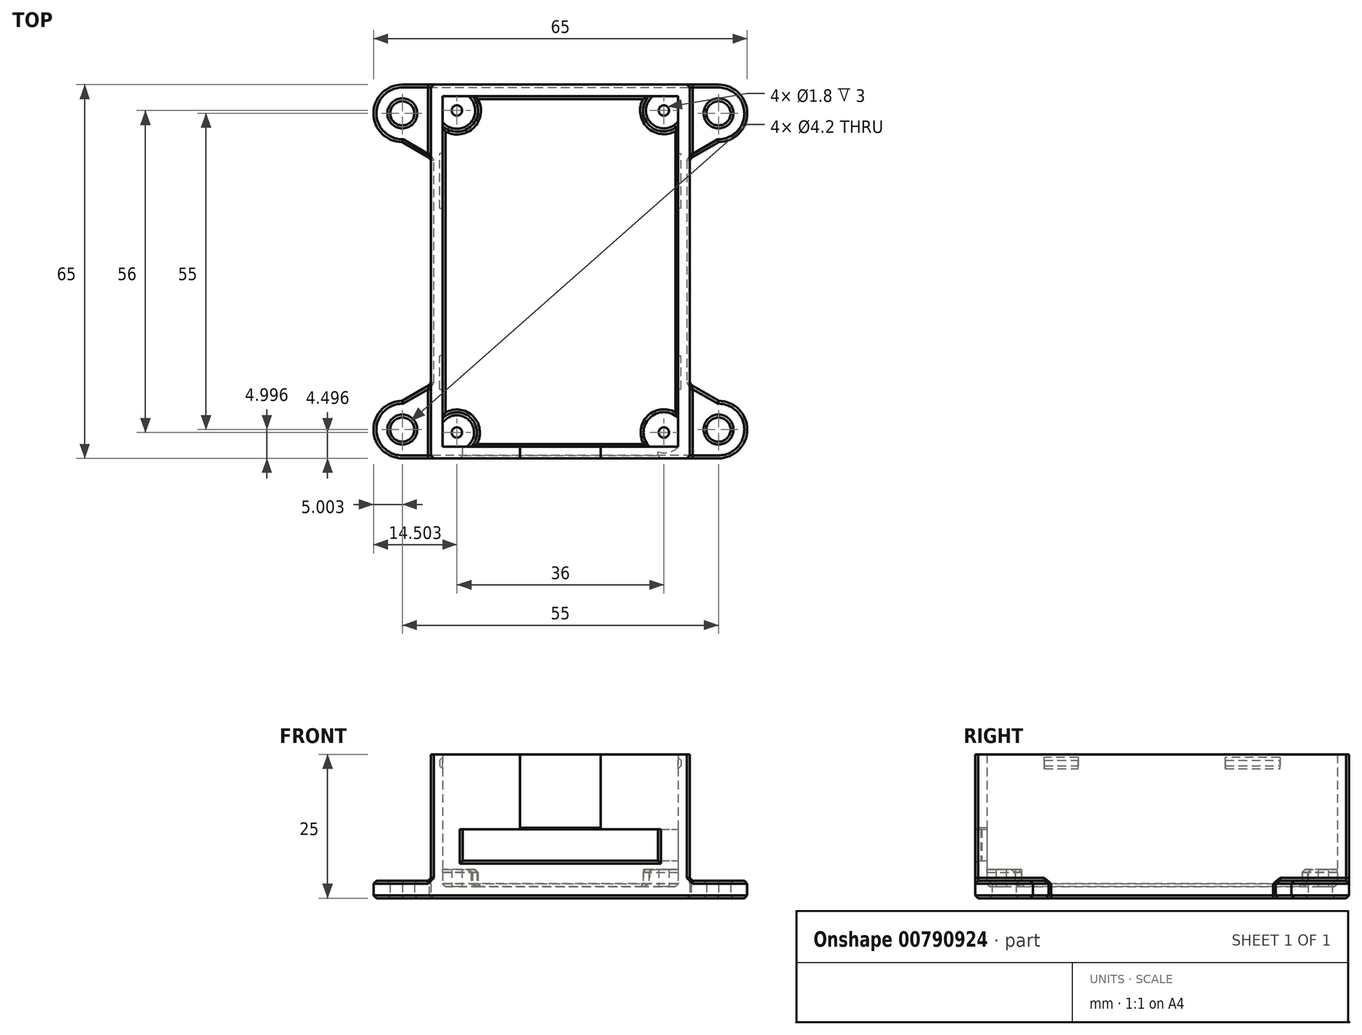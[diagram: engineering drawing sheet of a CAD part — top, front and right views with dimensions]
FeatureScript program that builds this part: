
annotation { "Feature Type Name" : "Feature", "Feature Type Description" : "" }
export const myFeature = defineFeature(function(context is Context, id is Id, definition is map)
    precondition{}
    {
        {
            var Q0;
            Q0=qCreatedBy(makeId("Top.planeOp"),FACE);
            var sketch = newSketch(context, id + "F0", { "sketchPlane" : qUnion([Q0])});
            skLineSegment(sketch, "E0.bottom", {"start": v(-31.58, 31.85) * mm, "end": v(9.42, 31.85) * mm});
            skLineSegment(sketch, "E0.top", {"start": v(-31.58, -29.15) * mm, "end": v(9.42, -29.15) * mm});
            skLineSegment(sketch, "E0.left", {"start": v(-31.58, 31.85) * mm, "end": v(-31.58, -29.15) * mm});
            skLineSegment(sketch, "E0.right", {"start": v(9.42, 31.85) * mm, "end": v(9.42, -29.15) * mm});
            skCircle(sketch, "E1", {"center": v(-29.08, 29.35) * mm, "radius": 0.9 * mm});
            skCircle(sketch, "E2", {"center": v(6.92, 29.35) * mm, "radius": 0.9 * mm});
            skCircle(sketch, "E3", {"center": v(-29.08, 29.35) * mm, "radius": 3.69 * mm});
            skCircle(sketch, "E4", {"center": v(6.92, 29.35) * mm, "radius": 3.62 * mm});
            skCircle(sketch, "E5", {"center": v(-29.08, -26.65) * mm, "radius": 0.9 * mm});
            skCircle(sketch, "E6", {"center": v(6.92, -26.65) * mm, "radius": 0.9 * mm});
            skCircle(sketch, "E7", {"center": v(-29.08, -26.65) * mm, "radius": 3.5 * mm});
            skCircle(sketch, "E8", {"center": v(6.92, -26.65) * mm, "radius": 3.54 * mm});
            skLineSegment(sketch, "E9.bottom", {"start": v(-33.58, 33.85) * mm, "end": v(11.42, 33.85) * mm});
            skLineSegment(sketch, "E9.top", {"start": v(-33.58, -31.15) * mm, "end": v(11.42, -31.15) * mm});
            skLineSegment(sketch, "E9.left", {"start": v(-33.58, 33.85) * mm, "end": v(-33.58, -31.15) * mm});
            skLineSegment(sketch, "E9.right", {"start": v(11.42, 33.85) * mm, "end": v(11.42, -31.15) * mm});
            skLineSegment(sketch, "E10.bottom", {"start": v(-32.08, -19.15) * mm, "end": v(9.92, -19.15) * mm});
            skLineSegment(sketch, "E10.top", {"start": v(-32.08, -13.29) * mm, "end": v(9.92, -13.29) * mm});
            skLineSegment(sketch, "E10.left", {"start": v(-32.08, -19.15) * mm, "end": v(-32.08, -13.29) * mm});
            skLineSegment(sketch, "E10.right", {"start": v(9.92, -19.15) * mm, "end": v(9.92, -13.29) * mm});
            skLineSegment(sketch, "E11.bottom", {"start": v(-32.08, 12.33) * mm, "end": v(9.92, 12.33) * mm});
            skLineSegment(sketch, "E11.top", {"start": v(-32.08, 21.85) * mm, "end": v(9.92, 21.85) * mm});
            skLineSegment(sketch, "E11.left", {"start": v(-32.08, 12.33) * mm, "end": v(-32.08, 21.85) * mm});
            skLineSegment(sketch, "E11.right", {"start": v(9.92, 12.33) * mm, "end": v(9.92, 21.85) * mm});
            skLineSegment(sketch, "E12.bottom", {"start": v(-28.08, -33.78) * mm, "end": v(5.92, -33.78) * mm});
            skLineSegment(sketch, "E12.top", {"start": v(-28.08, -29.15) * mm, "end": v(5.92, -29.15) * mm});
            skLineSegment(sketch, "E12.left", {"start": v(-28.08, -33.78) * mm, "end": v(-28.08, -29.15) * mm});
            skLineSegment(sketch, "E12.right", {"start": v(5.92, -33.78) * mm, "end": v(5.92, -29.15) * mm});
            skLineSegment(sketch, "E13.bottom", {"start": v(-18.08, -27.24) * mm, "end": v(-4.08, -27.24) * mm});
            skLineSegment(sketch, "E13.top", {"start": v(-18.08, -36.6) * mm, "end": v(-4.08, -36.6) * mm});
            skLineSegment(sketch, "E13.left", {"start": v(-18.08, -27.24) * mm, "end": v(-18.08, -36.6) * mm});
            skLineSegment(sketch, "E13.right", {"start": v(-4.08, -27.24) * mm, "end": v(-4.08, -36.6) * mm});
            skLineSegment(sketch, "E14", {"start": v(11.42, 33.85) * mm, "end": v(16.42, 33.85) * mm});
            skArc(sketch, "E15", {"start": v(16.42, 33.85) * mm, "mid": v(21.42, 28.85) * mm, "end": v(16.42, 23.85) * mm});
            skLineSegment(sketch, "E16", {"start": v(16.42, 23.85) * mm, "end": v(11.42, 20.96) * mm});
            skCircle(sketch, "E17", {"center": v(16.42, 28.85) * mm, "radius": 2.1 * mm});
            skLineSegment(sketch, "E18", {"start": v(-33.58, 33.85) * mm, "end": v(-38.58, 33.85) * mm});
            skArc(sketch, "E19", {"start": v(-38.58, 33.85) * mm, "mid": v(-43.58, 28.85) * mm, "end": v(-38.58, 23.85) * mm});
            skLineSegment(sketch, "E20", {"start": v(-38.58, 23.85) * mm, "end": v(-33.58, 20.96) * mm});
            skLineSegment(sketch, "E21", {"start": v(11.42, -31.15) * mm, "end": v(16.42, -31.15) * mm});
            skArc(sketch, "E22", {"start": v(16.42, -31.15) * mm, "mid": v(21.42, -26.15) * mm, "end": v(16.42, -21.15) * mm});
            skLineSegment(sketch, "E23", {"start": v(16.42, -21.15) * mm, "end": v(11.42, -18.27) * mm});
            skLineSegment(sketch, "E24", {"start": v(-33.58, -31.15) * mm, "end": v(-38.58, -31.15) * mm});
            skArc(sketch, "E25", {"start": v(-38.58, -31.15) * mm, "mid": v(-43.58, -26.15) * mm, "end": v(-38.58, -21.15) * mm});
            skLineSegment(sketch, "E26", {"start": v(-38.58, -21.15) * mm, "end": v(-33.58, -18.27) * mm});
            skCircle(sketch, "E27", {"center": v(-38.58, 28.85) * mm, "radius": 2.1 * mm});
            skCircle(sketch, "E28", {"center": v(-38.58, -26.15) * mm, "radius": 2.1 * mm});
            skCircle(sketch, "E29", {"center": v(16.42, -26.15) * mm, "radius": 2.1 * mm});
            skSolve(sketch);
        }
        {
            var Q0;
            Q0=makeQuery(id+"F0.imprint","IMPRINT",FACE,{"disambiguationData":[TD([[makeQuery(id+"F0.imprint","IMPRINT",EDGE,{"derivedFrom":sQuery(id+"F0.wireOp",EDGE,"E9.bottom")}),-1.0]])]});
            var Q1;
            {var subQ0=sQuery(id+"F0.wireOp",EDGE,"E0.right");var subQ1=sQuery(id+"F0.wireOp",EDGE,"E0.bottom");var subQ2=makeQuery(id+"F0.imprint","INTERSECT",VERTEX,{"derivedFrom":[subQ1,subQ0]});Q1=makeQuery(id+"F0.imprint","IMPRINT",FACE,{"disambiguationData":[TD([[makeQuery(id+"F0.imprint","IMPRINT",EDGE,{"disambiguationData":[TD([[subQ2,1.0]])],"derivedFrom":subQ1}),1.0]])]});}
            var Q2;
            {var subQ0=sQuery(id+"F0.wireOp",EDGE,"E7");var subQ1=sQuery(id+"F0.wireOp",EDGE,"E0.top");var subQ2=makeQuery(id+"F0.imprint","INTERSECT",VERTEX,{"disambiguationData":[OD(1.0)],"derivedFrom":[subQ1,subQ0]});Q2=makeQuery(id+"F0.imprint","IMPRINT",FACE,{"disambiguationData":[TD([[makeQuery(id+"F0.imprint","IMPRINT",EDGE,{"disambiguationData":[TD([[subQ2,-1.0]])],"derivedFrom":subQ1}),1.0]])]});}
            var Q3;
            {var subQ0=sQuery(id+"F0.wireOp",EDGE,"E13.right");var subQ1=sQuery(id+"F0.wireOp",EDGE,"E0.top");var subQ2=makeQuery(id+"F0.imprint","INTERSECT",VERTEX,{"derivedFrom":[subQ1,subQ0]});Q3=makeQuery(id+"F0.imprint","IMPRINT",FACE,{"disambiguationData":[TD([[makeQuery(id+"F0.imprint","IMPRINT",EDGE,{"disambiguationData":[TD([[subQ2,-1.0]])],"derivedFrom":subQ1}),1.0]])]});}
            var Q4;
            Q4=makeQuery(id+"F0.imprint","IMPRINT",FACE,{"disambiguationData":[TD([[makeQuery(id+"F0.imprint","IMPRINT",EDGE,{"derivedFrom":sQuery(id+"F0.wireOp",EDGE,"E5")}),-1.0]])]});
            var Q5;
            Q5=makeQuery(id+"F0.imprint","IMPRINT",FACE,{"disambiguationData":[TD([[makeQuery(id+"F0.imprint","IMPRINT",EDGE,{"derivedFrom":sQuery(id+"F0.wireOp",EDGE,"E1")}),-1.0]])]});
            var Q6;
            {var subQ0=sQuery(id+"F0.wireOp",EDGE,"E0.left");var subQ1=sQuery(id+"F0.wireOp",EDGE,"E0.bottom");var subQ2=makeQuery(id+"F0.imprint","INTERSECT",VERTEX,{"derivedFrom":[subQ1,subQ0]});Q6=makeQuery(id+"F0.imprint","IMPRINT",FACE,{"disambiguationData":[TD([[makeQuery(id+"F0.imprint","IMPRINT",EDGE,{"disambiguationData":[TD([[subQ2,-1.0]])],"derivedFrom":subQ1}),1.0]])]});}
            var Q7;
            {var subQ0=sQuery(id+"F0.wireOp",EDGE,"E13.left");var subQ1=sQuery(id+"F0.wireOp",EDGE,"E0.top");var subQ2=makeQuery(id+"F0.imprint","INTERSECT",VERTEX,{"derivedFrom":[subQ1,subQ0]});Q7=makeQuery(id+"F0.imprint","IMPRINT",FACE,{"disambiguationData":[TD([[makeQuery(id+"F0.imprint","IMPRINT",EDGE,{"disambiguationData":[TD([[subQ2,-1.0]])],"derivedFrom":subQ1}),-1.0]])]});}
            var Q8;
            {var subQ0=sQuery(id+"F0.wireOp",EDGE,"E11.top");var subQ1=sQuery(id+"F0.wireOp",EDGE,"E0.left");var subQ2=makeQuery(id+"F0.imprint","INTERSECT",VERTEX,{"derivedFrom":[subQ1,subQ0]});Q8=makeQuery(id+"F0.imprint","IMPRINT",FACE,{"disambiguationData":[TD([[makeQuery(id+"F0.imprint","IMPRINT",EDGE,{"disambiguationData":[TD([[subQ2,-1.0]])],"derivedFrom":subQ1}),1.0]])]});}
            var Q9;
            {var subQ3=sQuery(id+"F0.wireOp",EDGE,"E7");var subQ6=sQuery(id+"F0.wireOp",EDGE,"E0.top");var subQ9=makeQuery(id+"F0.imprint","INTERSECT",VERTEX,{"disambiguationData":[OD(1.0)],"derivedFrom":[subQ6,subQ3]});Q9=makeQuery(id+"F0.imprint","IMPRINT",FACE,{"disambiguationData":[TD([[makeQuery(id+"F0.imprint","IMPRINT",EDGE,{"disambiguationData":[TD([[subQ9,-1.0]])],"derivedFrom":subQ6}),-1.0]])]});}
            var Q10;
            Q10=makeQuery(id+"F0.imprint","IMPRINT",FACE,{"disambiguationData":[TD([[makeQuery(id+"F0.imprint","IMPRINT",EDGE,{"derivedFrom":sQuery(id+"F0.wireOp",EDGE,"E2")}),-1.0]])]});
            var Q11;
            {var subQ0=sQuery(id+"F0.wireOp",EDGE,"E10.top");var subQ1=sQuery(id+"F0.wireOp",EDGE,"E0.left");var subQ2=makeQuery(id+"F0.imprint","INTERSECT",VERTEX,{"derivedFrom":[subQ1,subQ0]});Q11=makeQuery(id+"F0.imprint","IMPRINT",FACE,{"disambiguationData":[TD([[makeQuery(id+"F0.imprint","IMPRINT",EDGE,{"disambiguationData":[TD([[subQ2,-1.0]])],"derivedFrom":subQ1}),1.0]])]});}
            var Q12;
            {var subQ5=sQuery(id+"F0.wireOp",EDGE,"E13.bottom");Q12=makeQuery(id+"F0.imprint","IMPRINT",FACE,{"disambiguationData":[TD([[makeQuery(id+"F0.imprint","IMPRINT",EDGE,{"derivedFrom":subQ5}),-1.0]])]});}
            var Q13;
            {var subQ0=sQuery(id+"F0.wireOp",EDGE,"E11.bottom");var subQ1=sQuery(id+"F0.wireOp",EDGE,"E0.left");var subQ2=makeQuery(id+"F0.imprint","INTERSECT",VERTEX,{"derivedFrom":[subQ1,subQ0]});Q13=makeQuery(id+"F0.imprint","IMPRINT",FACE,{"disambiguationData":[TD([[makeQuery(id+"F0.imprint","IMPRINT",EDGE,{"disambiguationData":[TD([[subQ2,-1.0]])],"derivedFrom":subQ1}),1.0]])]});}
            var Q14;
            {var subQ0=sQuery(id+"F0.wireOp",EDGE,"E13.left");var subQ1=sQuery(id+"F0.wireOp",EDGE,"E0.top");var subQ2=makeQuery(id+"F0.imprint","INTERSECT",VERTEX,{"derivedFrom":[subQ1,subQ0]});Q14=makeQuery(id+"F0.imprint","IMPRINT",FACE,{"disambiguationData":[TD([[makeQuery(id+"F0.imprint","IMPRINT",EDGE,{"disambiguationData":[TD([[subQ2,-1.0]])],"derivedFrom":subQ1}),1.0]])]});}
            var Q15;
            Q15=makeQuery(id+"F0.imprint","IMPRINT",FACE,{"disambiguationData":[TD([[makeQuery(id+"F0.imprint","IMPRINT",EDGE,{"derivedFrom":sQuery(id+"F0.wireOp",EDGE,"E6")}),-1.0]])]});
            var Q16;
            {var subQ14=sQuery(id+"F0.wireOp",EDGE,"E13.bottom");Q16=makeQuery(id+"F0.imprint","IMPRINT",FACE,{"disambiguationData":[TD([[makeQuery(id+"F0.imprint","IMPRINT",EDGE,{"derivedFrom":subQ14}),1.0]])]});}
            var Q17;
            {var subQ0=sQuery(id+"F0.wireOp",EDGE,"E3");var subQ1=sQuery(id+"F0.wireOp",EDGE,"E0.bottom");var subQ2=makeQuery(id+"F0.imprint","INTERSECT",VERTEX,{"derivedFrom":[subQ1,subQ0]});Q17=makeQuery(id+"F0.imprint","IMPRINT",FACE,{"disambiguationData":[TD([[makeQuery(id+"F0.imprint","IMPRINT",EDGE,{"disambiguationData":[TD([[subQ2,-1.0]])],"derivedFrom":subQ1}),-1.0]])]});}
            var Q18;
            {var subQ3=sQuery(id+"F0.wireOp",EDGE,"E13.right");var subQ7=sQuery(id+"F0.wireOp",EDGE,"E0.top");var subQ9=makeQuery(id+"F0.imprint","INTERSECT",VERTEX,{"derivedFrom":[subQ7,subQ3]});Q18=makeQuery(id+"F0.imprint","IMPRINT",FACE,{"disambiguationData":[TD([[makeQuery(id+"F0.imprint","IMPRINT",EDGE,{"disambiguationData":[TD([[subQ9,-1.0]])],"derivedFrom":subQ7}),-1.0]])]});}
            var Q19;
            {var subQ0=sQuery(id+"F0.wireOp",EDGE,"E7");var subQ1=sQuery(id+"F0.wireOp",EDGE,"E0.left");var subQ2=makeQuery(id+"F0.imprint","INTERSECT",VERTEX,{"disambiguationData":[OD(0.0)],"derivedFrom":[subQ1,subQ0]});Q19=makeQuery(id+"F0.imprint","IMPRINT",FACE,{"disambiguationData":[TD([[makeQuery(id+"F0.imprint","IMPRINT",EDGE,{"disambiguationData":[TD([[subQ2,-1.0]])],"derivedFrom":subQ1}),-1.0]])]});}
            var Q20;
            {var subQ0=sQuery(id+"F0.wireOp",EDGE,"E12.left");var subQ1=sQuery(id+"F0.wireOp",EDGE,"E0.top");var subQ2=makeQuery(id+"F0.imprint","INTERSECT",VERTEX,{"derivedFrom":[subQ1,subQ0]});Q20=makeQuery(id+"F0.imprint","IMPRINT",FACE,{"disambiguationData":[TD([[makeQuery(id+"F0.imprint","IMPRINT",EDGE,{"disambiguationData":[TD([[subQ2,-1.0]])],"derivedFrom":subQ1}),1.0]])]});}
            var Q21;
            {var subQ0=sQuery(id+"F0.wireOp",EDGE,"E8");var subQ1=sQuery(id+"F0.wireOp",EDGE,"E0.top");var subQ2=makeQuery(id+"F0.imprint","INTERSECT",VERTEX,{"derivedFrom":[subQ1,subQ0]});Q21=makeQuery(id+"F0.imprint","IMPRINT",FACE,{"disambiguationData":[TD([[makeQuery(id+"F0.imprint","IMPRINT",EDGE,{"disambiguationData":[TD([[subQ2,-1.0]])],"derivedFrom":subQ1}),-1.0]])]});}
            var Q22;
            {var subQ5=sQuery(id+"F0.wireOp",EDGE,"E11.right");Q22=makeQuery(id+"F0.imprint","IMPRINT",FACE,{"disambiguationData":[TD([[makeQuery(id+"F0.imprint","IMPRINT",EDGE,{"derivedFrom":subQ5}),1.0]])]});}
            var Q23;
            {var subQ5=sQuery(id+"F0.wireOp",EDGE,"E10.right");Q23=makeQuery(id+"F0.imprint","IMPRINT",FACE,{"disambiguationData":[TD([[makeQuery(id+"F0.imprint","IMPRINT",EDGE,{"derivedFrom":subQ5}),1.0]])]});}
            var Q24;
            {var subQ5=sQuery(id+"F0.wireOp",EDGE,"E10.left");Q24=makeQuery(id+"F0.imprint","IMPRINT",FACE,{"disambiguationData":[TD([[makeQuery(id+"F0.imprint","IMPRINT",EDGE,{"derivedFrom":subQ5}),-1.0]])]});}
            var Q25;
            {var subQ5=sQuery(id+"F0.wireOp",EDGE,"E11.left");Q25=makeQuery(id+"F0.imprint","IMPRINT",FACE,{"disambiguationData":[TD([[makeQuery(id+"F0.imprint","IMPRINT",EDGE,{"derivedFrom":subQ5}),-1.0]])]});}
            var Q26;
            {var subQ1=sQuery(id+"F0.wireOp",EDGE,"E0.top");var subQ3=sQuery(id+"F0.wireOp",EDGE,"E12.right");var subQ4=makeQuery(id+"F0.imprint","INTERSECT",VERTEX,{"derivedFrom":[subQ1,subQ3]});Q26=makeQuery(id+"F0.imprint","IMPRINT",FACE,{"disambiguationData":[TD([[makeQuery(id+"F0.imprint","IMPRINT",EDGE,{"disambiguationData":[TD([[subQ4,1.0]])],"derivedFrom":subQ3}),-1.0]])]});}
            var Q27;
            {var subQ0=sQuery(id+"F0.wireOp",EDGE,"E8");var subQ1=sQuery(id+"F0.wireOp",EDGE,"E0.right");var subQ3=makeQuery(id+"F0.imprint","INTERSECT",VERTEX,{"derivedFrom":[subQ1,subQ0]});Q27=makeQuery(id+"F0.imprint","IMPRINT",FACE,{"disambiguationData":[TD([[makeQuery(id+"F0.imprint","IMPRINT",EDGE,{"disambiguationData":[TD([[subQ3,-1.0]])],"derivedFrom":subQ1}),1.0]])]});}
            var Q28;
            {var subQ0=sQuery(id+"F0.wireOp",EDGE,"E12.left");var subQ1=sQuery(id+"F0.wireOp",EDGE,"E0.top");var subQ2=makeQuery(id+"F0.imprint","INTERSECT",VERTEX,{"derivedFrom":[subQ1,subQ0]});Q28=makeQuery(id+"F0.imprint","IMPRINT",FACE,{"disambiguationData":[TD([[makeQuery(id+"F0.imprint","IMPRINT",EDGE,{"disambiguationData":[TD([[subQ2,-1.0]])],"derivedFrom":subQ1}),-1.0]])]});}
            var Q29;
            {var subQ0=sQuery(id+"F0.wireOp",EDGE,"E8");var subQ1=sQuery(id+"F0.wireOp",EDGE,"E0.top");var subQ2=makeQuery(id+"F0.imprint","INTERSECT",VERTEX,{"derivedFrom":[subQ1,subQ0]});Q29=makeQuery(id+"F0.imprint","IMPRINT",FACE,{"disambiguationData":[TD([[makeQuery(id+"F0.imprint","IMPRINT",EDGE,{"disambiguationData":[TD([[subQ2,-1.0]])],"derivedFrom":subQ1}),1.0]])]});}
            var Q30;
            {var subQ0=sQuery(id+"F0.wireOp",EDGE,"E7");var subQ1=sQuery(id+"F0.wireOp",EDGE,"E0.top");var subQ2=makeQuery(id+"F0.imprint","INTERSECT",VERTEX,{"disambiguationData":[OD(0.0)],"derivedFrom":[subQ1,subQ0]});Q30=makeQuery(id+"F0.imprint","IMPRINT",FACE,{"disambiguationData":[TD([[makeQuery(id+"F0.imprint","IMPRINT",EDGE,{"disambiguationData":[TD([[subQ2,-1.0]])],"derivedFrom":subQ1}),-1.0]])]});}
            var Q31;
            {var subQ0=sQuery(id+"F0.wireOp",EDGE,"E0.left");var subQ1=sQuery(id+"F0.wireOp",EDGE,"E0.top");var subQ2=makeQuery(id+"F0.imprint","INTERSECT",VERTEX,{"derivedFrom":[subQ1,subQ0]});Q31=makeQuery(id+"F0.imprint","IMPRINT",FACE,{"disambiguationData":[TD([[makeQuery(id+"F0.imprint","IMPRINT",EDGE,{"disambiguationData":[TD([[subQ2,-1.0]])],"derivedFrom":subQ1}),1.0]])]});}
            var Q32;
            Q32=makeQuery(id+"F0.imprint","IMPRINT",FACE,{"disambiguationData":[TD([[makeQuery(id+"F0.imprint","IMPRINT",EDGE,{"derivedFrom":sQuery(id+"F0.wireOp",EDGE,"E6")}),1.0]])]});
            var Q33;
            Q33=makeQuery(id+"F0.imprint","IMPRINT",FACE,{"disambiguationData":[TD([[makeQuery(id+"F0.imprint","IMPRINT",EDGE,{"derivedFrom":sQuery(id+"F0.wireOp",EDGE,"E5")}),1.0]])]});
            var Q34;
            Q34=makeQuery(id+"F0.imprint","IMPRINT",FACE,{"disambiguationData":[TD([[makeQuery(id+"F0.imprint","IMPRINT",EDGE,{"derivedFrom":sQuery(id+"F0.wireOp",EDGE,"E2")}),1.0]])]});
            var Q35;
            Q35=makeQuery(id+"F0.imprint","IMPRINT",FACE,{"disambiguationData":[TD([[makeQuery(id+"F0.imprint","IMPRINT",EDGE,{"derivedFrom":sQuery(id+"F0.wireOp",EDGE,"E1")}),1.0]])]});
            var Q36;
            {var subQ0=sQuery(id+"F0.wireOp",EDGE,"E12.left");var subQ3=sQuery(id+"F0.wireOp",EDGE,"E7");var subQ4=makeQuery(id+"F0.imprint","INTERSECT",VERTEX,{"derivedFrom":[subQ3,subQ0]});Q36=makeQuery(id+"F0.imprint","IMPRINT",FACE,{"disambiguationData":[TD([[makeQuery(id+"F0.imprint","IMPRINT",EDGE,{"disambiguationData":[TD([[subQ4,-1.0]])],"derivedFrom":subQ3}),-1.0]])]});}
            var Q37;
            {var subQ0=sQuery(id+"F0.wireOp",EDGE,"E13.left");var subQ1=sQuery(id+"F0.wireOp",EDGE,"E9.top");var subQ2=makeQuery(id+"F0.imprint","INTERSECT",VERTEX,{"derivedFrom":[subQ1,subQ0]});Q37=makeQuery(id+"F0.imprint","IMPRINT",FACE,{"disambiguationData":[TD([[makeQuery(id+"F0.imprint","IMPRINT",EDGE,{"disambiguationData":[TD([[subQ2,-1.0]])],"derivedFrom":subQ1}),1.0]])]});}
            var Q38;
            {var subQ3=sQuery(id+"F0.wireOp",EDGE,"E8");var subQ7=sQuery(id+"F0.wireOp",EDGE,"E12.top");var subQ9=makeQuery(id+"F0.imprint","INTERSECT",VERTEX,{"derivedFrom":[subQ3,subQ7]});Q38=makeQuery(id+"F0.imprint","IMPRINT",FACE,{"disambiguationData":[TD([[makeQuery(id+"F0.imprint","IMPRINT",EDGE,{"disambiguationData":[TD([[subQ9,-1.0]])],"derivedFrom":subQ3}),-1.0]])]});}
            var Q39;
            {var subQ0=sQuery(id+"F0.wireOp",EDGE,"E12.left");var subQ1=sQuery(id+"F0.wireOp",EDGE,"E7");var subQ2=makeQuery(id+"F0.imprint","INTERSECT",VERTEX,{"derivedFrom":[subQ1,subQ0]});Q39=makeQuery(id+"F0.imprint","IMPRINT",FACE,{"disambiguationData":[TD([[makeQuery(id+"F0.imprint","IMPRINT",EDGE,{"disambiguationData":[TD([[subQ2,-1.0]])],"derivedFrom":subQ1}),1.0]])]});}
            var Q40;
            {var subQ0=sQuery(id+"F0.wireOp",EDGE,"E12.top");var subQ1=sQuery(id+"F0.wireOp",EDGE,"E8");var subQ2=makeQuery(id+"F0.imprint","INTERSECT",VERTEX,{"derivedFrom":[subQ1,subQ0]});Q40=makeQuery(id+"F0.imprint","IMPRINT",FACE,{"disambiguationData":[TD([[makeQuery(id+"F0.imprint","IMPRINT",EDGE,{"disambiguationData":[TD([[subQ2,-1.0]])],"derivedFrom":subQ1}),1.0]])]});}
            extrude(context, id + "F1", {"entities" : qUnion([Q0, Q1, Q2, Q3, Q4, Q5, Q6, Q7, Q8, Q9, Q10, Q11, Q12, Q13, Q14, Q15, Q16, Q17, Q18, Q19, Q20, Q21, Q22, Q23, Q24, Q25, Q26, Q27, Q28, Q29, Q30, Q31, Q32, Q33, Q34, Q35, Q36, Q37, Q38, Q39, Q40]), "depth" : 25 * mm, "offsetDistance" : 25 * mm});
        }
        {
            var Q0;
            {var subQ0=sQuery(id+"F0.wireOp",EDGE,"E3");var subQ1=sQuery(id+"F0.wireOp",EDGE,"E0.bottom");var subQ2=makeQuery(id+"F0.imprint","INTERSECT",VERTEX,{"derivedFrom":[subQ1,subQ0]});Q0=makeQuery(id+"F0.imprint","IMPRINT",FACE,{"disambiguationData":[TD([[makeQuery(id+"F0.imprint","IMPRINT",EDGE,{"disambiguationData":[TD([[subQ2,-1.0]])],"derivedFrom":subQ1}),-1.0]])]});}
            var Q1;
            {var subQ0=sQuery(id+"F0.wireOp",EDGE,"E11.top");var subQ1=sQuery(id+"F0.wireOp",EDGE,"E0.left");var subQ2=makeQuery(id+"F0.imprint","INTERSECT",VERTEX,{"derivedFrom":[subQ1,subQ0]});Q1=makeQuery(id+"F0.imprint","IMPRINT",FACE,{"disambiguationData":[TD([[makeQuery(id+"F0.imprint","IMPRINT",EDGE,{"disambiguationData":[TD([[subQ2,-1.0]])],"derivedFrom":subQ1}),1.0]])]});}
            var Q2;
            {var subQ0=sQuery(id+"F0.wireOp",EDGE,"E11.bottom");var subQ1=sQuery(id+"F0.wireOp",EDGE,"E0.left");var subQ2=makeQuery(id+"F0.imprint","INTERSECT",VERTEX,{"derivedFrom":[subQ1,subQ0]});Q2=makeQuery(id+"F0.imprint","IMPRINT",FACE,{"disambiguationData":[TD([[makeQuery(id+"F0.imprint","IMPRINT",EDGE,{"disambiguationData":[TD([[subQ2,-1.0]])],"derivedFrom":subQ1}),1.0]])]});}
            var Q3;
            {var subQ0=sQuery(id+"F0.wireOp",EDGE,"E10.top");var subQ1=sQuery(id+"F0.wireOp",EDGE,"E0.left");var subQ2=makeQuery(id+"F0.imprint","INTERSECT",VERTEX,{"derivedFrom":[subQ1,subQ0]});Q3=makeQuery(id+"F0.imprint","IMPRINT",FACE,{"disambiguationData":[TD([[makeQuery(id+"F0.imprint","IMPRINT",EDGE,{"disambiguationData":[TD([[subQ2,-1.0]])],"derivedFrom":subQ1}),1.0]])]});}
            var Q4;
            {var subQ14=sQuery(id+"F0.wireOp",EDGE,"E13.bottom");Q4=makeQuery(id+"F0.imprint","IMPRINT",FACE,{"disambiguationData":[TD([[makeQuery(id+"F0.imprint","IMPRINT",EDGE,{"derivedFrom":subQ14}),1.0]])]});}
            var Q5;
            {var subQ5=sQuery(id+"F0.wireOp",EDGE,"E13.bottom");Q5=makeQuery(id+"F0.imprint","IMPRINT",FACE,{"disambiguationData":[TD([[makeQuery(id+"F0.imprint","IMPRINT",EDGE,{"derivedFrom":subQ5}),-1.0]])]});}
            var Q6;
            {var subQ0=sQuery(id+"F0.wireOp",EDGE,"E13.left");var subQ1=sQuery(id+"F0.wireOp",EDGE,"E0.top");var subQ2=makeQuery(id+"F0.imprint","INTERSECT",VERTEX,{"derivedFrom":[subQ1,subQ0]});Q6=makeQuery(id+"F0.imprint","IMPRINT",FACE,{"disambiguationData":[TD([[makeQuery(id+"F0.imprint","IMPRINT",EDGE,{"disambiguationData":[TD([[subQ2,-1.0]])],"derivedFrom":subQ1}),1.0]])]});}
            var Q7;
            {var subQ0=sQuery(id+"F0.wireOp",EDGE,"E13.right");var subQ1=sQuery(id+"F0.wireOp",EDGE,"E0.top");var subQ2=makeQuery(id+"F0.imprint","INTERSECT",VERTEX,{"derivedFrom":[subQ1,subQ0]});Q7=makeQuery(id+"F0.imprint","IMPRINT",FACE,{"disambiguationData":[TD([[makeQuery(id+"F0.imprint","IMPRINT",EDGE,{"disambiguationData":[TD([[subQ2,-1.0]])],"derivedFrom":subQ1}),1.0]])]});}
            var Q8;
            Q8=makeQuery(id+"F0.imprint","IMPRINT",FACE,{"disambiguationData":[TD([[makeQuery(id+"F0.imprint","IMPRINT",EDGE,{"derivedFrom":sQuery(id+"F0.wireOp",EDGE,"E6")}),1.0]])]});
            var Q9;
            Q9=makeQuery(id+"F0.imprint","IMPRINT",FACE,{"disambiguationData":[TD([[makeQuery(id+"F0.imprint","IMPRINT",EDGE,{"derivedFrom":sQuery(id+"F0.wireOp",EDGE,"E5")}),1.0]])]});
            var Q10;
            Q10=makeQuery(id+"F0.imprint","IMPRINT",FACE,{"disambiguationData":[TD([[makeQuery(id+"F0.imprint","IMPRINT",EDGE,{"derivedFrom":sQuery(id+"F0.wireOp",EDGE,"E2")}),1.0]])]});
            var Q11;
            Q11=makeQuery(id+"F0.imprint","IMPRINT",FACE,{"disambiguationData":[TD([[makeQuery(id+"F0.imprint","IMPRINT",EDGE,{"derivedFrom":sQuery(id+"F0.wireOp",EDGE,"E1")}),1.0]])]});
            extrude(context, id + "F2", {"entities" : qUnion([Q0, Q1, Q2, Q3, Q4, Q5, Q6, Q7, Q8, Q9, Q10, Q11]), "operationType" : NewBodyOperationType.REMOVE, "depth" : 5 * mm, "offsetDistance" : 25 * mm, "hasSecondDirection" : true, "secondDirectionOppositeDirection" : false, "secondDirectionDepth" : 2 * mm});
        }
        {
            var Q0;
            Q0=makeQuery(id+"F0.imprint","IMPRINT",FACE,{"disambiguationData":[TD([[makeQuery(id+"F0.imprint","IMPRINT",EDGE,{"derivedFrom":sQuery(id+"F0.wireOp",EDGE,"E5")}),-1.0]])]});
            var Q1;
            Q1=makeQuery(id+"F0.imprint","IMPRINT",FACE,{"disambiguationData":[TD([[makeQuery(id+"F0.imprint","IMPRINT",EDGE,{"derivedFrom":sQuery(id+"F0.wireOp",EDGE,"E1")}),-1.0]])]});
            var Q2;
            {var subQ0=sQuery(id+"F0.wireOp",EDGE,"E11.top");var subQ1=sQuery(id+"F0.wireOp",EDGE,"E0.left");var subQ2=makeQuery(id+"F0.imprint","INTERSECT",VERTEX,{"derivedFrom":[subQ1,subQ0]});Q2=makeQuery(id+"F0.imprint","IMPRINT",FACE,{"disambiguationData":[TD([[makeQuery(id+"F0.imprint","IMPRINT",EDGE,{"disambiguationData":[TD([[subQ2,-1.0]])],"derivedFrom":subQ1}),1.0]])]});}
            var Q3;
            Q3=makeQuery(id+"F0.imprint","IMPRINT",FACE,{"disambiguationData":[TD([[makeQuery(id+"F0.imprint","IMPRINT",EDGE,{"derivedFrom":sQuery(id+"F0.wireOp",EDGE,"E2")}),-1.0]])]});
            var Q4;
            {var subQ0=sQuery(id+"F0.wireOp",EDGE,"E10.top");var subQ1=sQuery(id+"F0.wireOp",EDGE,"E0.left");var subQ2=makeQuery(id+"F0.imprint","INTERSECT",VERTEX,{"derivedFrom":[subQ1,subQ0]});Q4=makeQuery(id+"F0.imprint","IMPRINT",FACE,{"disambiguationData":[TD([[makeQuery(id+"F0.imprint","IMPRINT",EDGE,{"disambiguationData":[TD([[subQ2,-1.0]])],"derivedFrom":subQ1}),1.0]])]});}
            var Q5;
            {var subQ5=sQuery(id+"F0.wireOp",EDGE,"E13.bottom");Q5=makeQuery(id+"F0.imprint","IMPRINT",FACE,{"disambiguationData":[TD([[makeQuery(id+"F0.imprint","IMPRINT",EDGE,{"derivedFrom":subQ5}),-1.0]])]});}
            var Q6;
            {var subQ0=sQuery(id+"F0.wireOp",EDGE,"E11.bottom");var subQ1=sQuery(id+"F0.wireOp",EDGE,"E0.left");var subQ2=makeQuery(id+"F0.imprint","INTERSECT",VERTEX,{"derivedFrom":[subQ1,subQ0]});Q6=makeQuery(id+"F0.imprint","IMPRINT",FACE,{"disambiguationData":[TD([[makeQuery(id+"F0.imprint","IMPRINT",EDGE,{"disambiguationData":[TD([[subQ2,-1.0]])],"derivedFrom":subQ1}),1.0]])]});}
            var Q7;
            Q7=makeQuery(id+"F0.imprint","IMPRINT",FACE,{"disambiguationData":[TD([[makeQuery(id+"F0.imprint","IMPRINT",EDGE,{"derivedFrom":sQuery(id+"F0.wireOp",EDGE,"E6")}),-1.0]])]});
            var Q8;
            {var subQ14=sQuery(id+"F0.wireOp",EDGE,"E13.bottom");Q8=makeQuery(id+"F0.imprint","IMPRINT",FACE,{"disambiguationData":[TD([[makeQuery(id+"F0.imprint","IMPRINT",EDGE,{"derivedFrom":subQ14}),1.0]])]});}
            var Q9;
            {var subQ0=sQuery(id+"F0.wireOp",EDGE,"E3");var subQ1=sQuery(id+"F0.wireOp",EDGE,"E0.bottom");var subQ2=makeQuery(id+"F0.imprint","INTERSECT",VERTEX,{"derivedFrom":[subQ1,subQ0]});Q9=makeQuery(id+"F0.imprint","IMPRINT",FACE,{"disambiguationData":[TD([[makeQuery(id+"F0.imprint","IMPRINT",EDGE,{"disambiguationData":[TD([[subQ2,-1.0]])],"derivedFrom":subQ1}),-1.0]])]});}
            var Q10;
            {var subQ0=sQuery(id+"F0.wireOp",EDGE,"E7");var subQ1=sQuery(id+"F0.wireOp",EDGE,"E0.top");var subQ2=makeQuery(id+"F0.imprint","INTERSECT",VERTEX,{"disambiguationData":[OD(1.0)],"derivedFrom":[subQ1,subQ0]});Q10=makeQuery(id+"F0.imprint","IMPRINT",FACE,{"disambiguationData":[TD([[makeQuery(id+"F0.imprint","IMPRINT",EDGE,{"disambiguationData":[TD([[subQ2,-1.0]])],"derivedFrom":subQ1}),1.0]])]});}
            var Q11;
            {var subQ0=sQuery(id+"F0.wireOp",EDGE,"E13.right");var subQ1=sQuery(id+"F0.wireOp",EDGE,"E0.top");var subQ2=makeQuery(id+"F0.imprint","INTERSECT",VERTEX,{"derivedFrom":[subQ1,subQ0]});Q11=makeQuery(id+"F0.imprint","IMPRINT",FACE,{"disambiguationData":[TD([[makeQuery(id+"F0.imprint","IMPRINT",EDGE,{"disambiguationData":[TD([[subQ2,-1.0]])],"derivedFrom":subQ1}),1.0]])]});}
            var Q12;
            {var subQ0=sQuery(id+"F0.wireOp",EDGE,"E13.left");var subQ1=sQuery(id+"F0.wireOp",EDGE,"E0.top");var subQ2=makeQuery(id+"F0.imprint","INTERSECT",VERTEX,{"derivedFrom":[subQ1,subQ0]});Q12=makeQuery(id+"F0.imprint","IMPRINT",FACE,{"disambiguationData":[TD([[makeQuery(id+"F0.imprint","IMPRINT",EDGE,{"disambiguationData":[TD([[subQ2,-1.0]])],"derivedFrom":subQ1}),1.0]])]});}
            var Q13;
            {var subQ0=sQuery(id+"F0.wireOp",EDGE,"E8");var subQ1=sQuery(id+"F0.wireOp",EDGE,"E0.top");var subQ2=makeQuery(id+"F0.imprint","INTERSECT",VERTEX,{"derivedFrom":[subQ1,subQ0]});Q13=makeQuery(id+"F0.imprint","IMPRINT",FACE,{"disambiguationData":[TD([[makeQuery(id+"F0.imprint","IMPRINT",EDGE,{"disambiguationData":[TD([[subQ2,-1.0]])],"derivedFrom":subQ1}),1.0]])]});}
            var Q14;
            {var subQ0=sQuery(id+"F0.wireOp",EDGE,"E12.left");var subQ1=sQuery(id+"F0.wireOp",EDGE,"E0.top");var subQ2=makeQuery(id+"F0.imprint","INTERSECT",VERTEX,{"derivedFrom":[subQ1,subQ0]});Q14=makeQuery(id+"F0.imprint","IMPRINT",FACE,{"disambiguationData":[TD([[makeQuery(id+"F0.imprint","IMPRINT",EDGE,{"disambiguationData":[TD([[subQ2,-1.0]])],"derivedFrom":subQ1}),1.0]])]});}
            var Q15;
            {var subQ0=sQuery(id+"F0.wireOp",EDGE,"E0.left");var subQ1=sQuery(id+"F0.wireOp",EDGE,"E0.top");var subQ2=makeQuery(id+"F0.imprint","INTERSECT",VERTEX,{"derivedFrom":[subQ1,subQ0]});Q15=makeQuery(id+"F0.imprint","IMPRINT",FACE,{"disambiguationData":[TD([[makeQuery(id+"F0.imprint","IMPRINT",EDGE,{"disambiguationData":[TD([[subQ2,-1.0]])],"derivedFrom":subQ1}),1.0]])]});}
            var Q16;
            Q16=makeQuery(id+"F0.imprint","IMPRINT",FACE,{"disambiguationData":[TD([[makeQuery(id+"F0.imprint","IMPRINT",EDGE,{"derivedFrom":sQuery(id+"F0.wireOp",EDGE,"E6")}),1.0]])]});
            var Q17;
            Q17=makeQuery(id+"F0.imprint","IMPRINT",FACE,{"disambiguationData":[TD([[makeQuery(id+"F0.imprint","IMPRINT",EDGE,{"derivedFrom":sQuery(id+"F0.wireOp",EDGE,"E5")}),1.0]])]});
            var Q18;
            Q18=makeQuery(id+"F0.imprint","IMPRINT",FACE,{"disambiguationData":[TD([[makeQuery(id+"F0.imprint","IMPRINT",EDGE,{"derivedFrom":sQuery(id+"F0.wireOp",EDGE,"E2")}),1.0]])]});
            var Q19;
            Q19=makeQuery(id+"F0.imprint","IMPRINT",FACE,{"disambiguationData":[TD([[makeQuery(id+"F0.imprint","IMPRINT",EDGE,{"derivedFrom":sQuery(id+"F0.wireOp",EDGE,"E1")}),1.0]])]});
            extrude(context, id + "F3", {"entities" : qUnion([Q0, Q1, Q2, Q3, Q4, Q5, Q6, Q7, Q8, Q9, Q10, Q11, Q12, Q13, Q14, Q15, Q16, Q17, Q18, Q19]), "operationType" : NewBodyOperationType.REMOVE, "depth" : 25 * mm, "offsetDistance" : 25 * mm, "hasSecondDirection" : true, "secondDirectionOppositeDirection" : false, "secondDirectionDepth" : 5 * mm});
        }
        {
            var Q0;
            {var subQ0=sQuery(id+"F0.wireOp",EDGE,"E8");var subQ1=sQuery(id+"F0.wireOp",EDGE,"E0.top");var subQ2=makeQuery(id+"F0.imprint","INTERSECT",VERTEX,{"derivedFrom":[subQ1,subQ0]});Q0=makeQuery(id+"F0.imprint","IMPRINT",FACE,{"disambiguationData":[TD([[makeQuery(id+"F0.imprint","IMPRINT",EDGE,{"disambiguationData":[TD([[subQ2,-1.0]])],"derivedFrom":subQ1}),-1.0]])]});}
            var Q1;
            {var subQ0=sQuery(id+"F0.wireOp",EDGE,"E12.right");var subQ1=sQuery(id+"F0.wireOp",EDGE,"E9.top");var subQ2=makeQuery(id+"F0.imprint","INTERSECT",VERTEX,{"derivedFrom":[subQ1,subQ0]});Q1=makeQuery(id+"F0.imprint","IMPRINT",FACE,{"disambiguationData":[TD([[makeQuery(id+"F0.imprint","IMPRINT",EDGE,{"disambiguationData":[TD([[subQ2,1.0]])],"derivedFrom":subQ1}),-1.0]])]});}
            var Q2;
            {var subQ0=sQuery(id+"F0.wireOp",EDGE,"E13.left");var subQ1=sQuery(id+"F0.wireOp",EDGE,"E9.top");var subQ2=makeQuery(id+"F0.imprint","INTERSECT",VERTEX,{"derivedFrom":[subQ1,subQ0]});Q2=makeQuery(id+"F0.imprint","IMPRINT",FACE,{"disambiguationData":[TD([[makeQuery(id+"F0.imprint","IMPRINT",EDGE,{"disambiguationData":[TD([[subQ2,-1.0]])],"derivedFrom":subQ1}),-1.0]])]});}
            var Q3;
            {var subQ0=sQuery(id+"F0.wireOp",EDGE,"E12.left");var subQ1=sQuery(id+"F0.wireOp",EDGE,"E9.top");var subQ2=makeQuery(id+"F0.imprint","INTERSECT",VERTEX,{"derivedFrom":[subQ1,subQ0]});Q3=makeQuery(id+"F0.imprint","IMPRINT",FACE,{"disambiguationData":[TD([[makeQuery(id+"F0.imprint","IMPRINT",EDGE,{"disambiguationData":[TD([[subQ2,-1.0]])],"derivedFrom":subQ1}),-1.0]])]});}
            var Q4;
            {var subQ0=sQuery(id+"F0.wireOp",EDGE,"E12.left");var subQ1=sQuery(id+"F0.wireOp",EDGE,"E0.top");var subQ2=makeQuery(id+"F0.imprint","INTERSECT",VERTEX,{"derivedFrom":[subQ1,subQ0]});Q4=makeQuery(id+"F0.imprint","IMPRINT",FACE,{"disambiguationData":[TD([[makeQuery(id+"F0.imprint","IMPRINT",EDGE,{"disambiguationData":[TD([[subQ2,-1.0]])],"derivedFrom":subQ1}),-1.0]])]});}
            var Q5;
            {var subQ0=sQuery(id+"F0.wireOp",EDGE,"E12.left");var subQ1=sQuery(id+"F0.wireOp",EDGE,"E0.top");var subQ2=makeQuery(id+"F0.imprint","INTERSECT",VERTEX,{"derivedFrom":[subQ1,subQ0]});Q5=makeQuery(id+"F0.imprint","IMPRINT",FACE,{"disambiguationData":[TD([[makeQuery(id+"F0.imprint","IMPRINT",EDGE,{"disambiguationData":[TD([[subQ2,-1.0]])],"derivedFrom":subQ1}),1.0]])]});}
            var Q6;
            {var subQ0=sQuery(id+"F0.wireOp",EDGE,"E8");var subQ1=sQuery(id+"F0.wireOp",EDGE,"E0.top");var subQ2=makeQuery(id+"F0.imprint","INTERSECT",VERTEX,{"derivedFrom":[subQ1,subQ0]});Q6=makeQuery(id+"F0.imprint","IMPRINT",FACE,{"disambiguationData":[TD([[makeQuery(id+"F0.imprint","IMPRINT",EDGE,{"disambiguationData":[TD([[subQ2,-1.0]])],"derivedFrom":subQ1}),1.0]])]});}
            var Q7;
            {var subQ0=sQuery(id+"F0.wireOp",EDGE,"E12.left");var subQ3=sQuery(id+"F0.wireOp",EDGE,"E7");var subQ4=makeQuery(id+"F0.imprint","INTERSECT",VERTEX,{"derivedFrom":[subQ3,subQ0]});Q7=makeQuery(id+"F0.imprint","IMPRINT",FACE,{"disambiguationData":[TD([[makeQuery(id+"F0.imprint","IMPRINT",EDGE,{"disambiguationData":[TD([[subQ4,-1.0]])],"derivedFrom":subQ3}),-1.0]])]});}
            var Q8;
            {var subQ0=sQuery(id+"F0.wireOp",EDGE,"E12.left");var subQ1=sQuery(id+"F0.wireOp",EDGE,"E7");var subQ2=makeQuery(id+"F0.imprint","INTERSECT",VERTEX,{"derivedFrom":[subQ1,subQ0]});Q8=makeQuery(id+"F0.imprint","IMPRINT",FACE,{"disambiguationData":[TD([[makeQuery(id+"F0.imprint","IMPRINT",EDGE,{"disambiguationData":[TD([[subQ2,-1.0]])],"derivedFrom":subQ1}),1.0]])]});}
            var Q9;
            {var subQ0=sQuery(id+"F0.wireOp",EDGE,"E13.left");var subQ1=sQuery(id+"F0.wireOp",EDGE,"E9.top");var subQ2=makeQuery(id+"F0.imprint","INTERSECT",VERTEX,{"derivedFrom":[subQ1,subQ0]});Q9=makeQuery(id+"F0.imprint","IMPRINT",FACE,{"disambiguationData":[TD([[makeQuery(id+"F0.imprint","IMPRINT",EDGE,{"disambiguationData":[TD([[subQ2,-1.0]])],"derivedFrom":subQ1}),1.0]])]});}
            var Q10;
            {var subQ3=sQuery(id+"F0.wireOp",EDGE,"E8");var subQ5=sQuery(id+"F0.wireOp",EDGE,"E12.top");var subQ6=makeQuery(id+"F0.imprint","INTERSECT",VERTEX,{"derivedFrom":[subQ3,subQ5]});Q10=makeQuery(id+"F0.imprint","IMPRINT",FACE,{"disambiguationData":[TD([[makeQuery(id+"F0.imprint","IMPRINT",EDGE,{"disambiguationData":[TD([[subQ6,-1.0]])],"derivedFrom":subQ3}),-1.0]])]});}
            var Q11;
            {var subQ0=sQuery(id+"F0.wireOp",EDGE,"E12.top");var subQ1=sQuery(id+"F0.wireOp",EDGE,"E8");var subQ2=makeQuery(id+"F0.imprint","INTERSECT",VERTEX,{"derivedFrom":[subQ1,subQ0]});Q11=makeQuery(id+"F0.imprint","IMPRINT",FACE,{"disambiguationData":[TD([[makeQuery(id+"F0.imprint","IMPRINT",EDGE,{"disambiguationData":[TD([[subQ2,-1.0]])],"derivedFrom":subQ1}),1.0]])]});}
            extrude(context, id + "F4", {"entities" : qUnion([Q0, Q1, Q2, Q3, Q4, Q5, Q6, Q7, Q8, Q9, Q10, Q11]), "operationType" : NewBodyOperationType.REMOVE, "depth" : 12 * mm, "offsetDistance" : 25 * mm, "hasSecondDirection" : true, "secondDirectionOppositeDirection" : false, "secondDirectionDepth" : 6.5 * mm});
        }
        {
            var Q0;
            {var subQ0=sQuery(id+"F0.wireOp",EDGE,"E13.left");var subQ1=sQuery(id+"F0.wireOp",EDGE,"E9.top");var subQ2=makeQuery(id+"F0.imprint","INTERSECT",VERTEX,{"derivedFrom":[subQ1,subQ0]});Q0=makeQuery(id+"F0.imprint","IMPRINT",FACE,{"disambiguationData":[TD([[makeQuery(id+"F0.imprint","IMPRINT",EDGE,{"disambiguationData":[TD([[subQ2,-1.0]])],"derivedFrom":subQ1}),-1.0]])]});}
            var Q1;
            {var subQ0=sQuery(id+"F0.wireOp",EDGE,"E13.left");var subQ1=sQuery(id+"F0.wireOp",EDGE,"E9.top");var subQ2=makeQuery(id+"F0.imprint","INTERSECT",VERTEX,{"derivedFrom":[subQ1,subQ0]});Q1=makeQuery(id+"F0.imprint","IMPRINT",FACE,{"disambiguationData":[TD([[makeQuery(id+"F0.imprint","IMPRINT",EDGE,{"disambiguationData":[TD([[subQ2,-1.0]])],"derivedFrom":subQ1}),1.0]])]});}
            extrude(context, id + "F5", {"entities" : qUnion([Q0, Q1]), "operationType" : NewBodyOperationType.REMOVE, "depth" : 25 * mm, "offsetDistance" : 25 * mm, "hasSecondDirection" : true, "secondDirectionOppositeDirection" : false, "secondDirectionDepth" : 12.2 * mm});
        }
        {
            var Q0;
            {var subQ0=sQuery(id+"F0.wireOp",EDGE,"E11.top");var subQ1=sQuery(id+"F0.wireOp",EDGE,"E0.left");var subQ2=makeQuery(id+"F0.imprint","INTERSECT",VERTEX,{"derivedFrom":[subQ1,subQ0]});Q0=makeQuery(id+"F0.imprint","IMPRINT",FACE,{"disambiguationData":[TD([[makeQuery(id+"F0.imprint","IMPRINT",EDGE,{"disambiguationData":[TD([[subQ2,-1.0]])],"derivedFrom":subQ1}),1.0]])]});}
            var Q1;
            {var subQ5=sQuery(id+"F0.wireOp",EDGE,"E11.left");Q1=makeQuery(id+"F0.imprint","IMPRINT",FACE,{"disambiguationData":[TD([[makeQuery(id+"F0.imprint","IMPRINT",EDGE,{"derivedFrom":subQ5}),-1.0]])]});}
            var Q2;
            {var subQ5=sQuery(id+"F0.wireOp",EDGE,"E11.right");Q2=makeQuery(id+"F0.imprint","IMPRINT",FACE,{"disambiguationData":[TD([[makeQuery(id+"F0.imprint","IMPRINT",EDGE,{"derivedFrom":subQ5}),1.0]])]});}
            var Q3;
            {var subQ5=sQuery(id+"F0.wireOp",EDGE,"E10.right");Q3=makeQuery(id+"F0.imprint","IMPRINT",FACE,{"disambiguationData":[TD([[makeQuery(id+"F0.imprint","IMPRINT",EDGE,{"derivedFrom":subQ5}),1.0]])]});}
            var Q4;
            {var subQ0=sQuery(id+"F0.wireOp",EDGE,"E10.top");var subQ1=sQuery(id+"F0.wireOp",EDGE,"E0.left");var subQ2=makeQuery(id+"F0.imprint","INTERSECT",VERTEX,{"derivedFrom":[subQ1,subQ0]});Q4=makeQuery(id+"F0.imprint","IMPRINT",FACE,{"disambiguationData":[TD([[makeQuery(id+"F0.imprint","IMPRINT",EDGE,{"disambiguationData":[TD([[subQ2,-1.0]])],"derivedFrom":subQ1}),1.0]])]});}
            var Q5;
            {var subQ5=sQuery(id+"F0.wireOp",EDGE,"E10.left");Q5=makeQuery(id+"F0.imprint","IMPRINT",FACE,{"disambiguationData":[TD([[makeQuery(id+"F0.imprint","IMPRINT",EDGE,{"derivedFrom":subQ5}),-1.0]])]});}
            extrude(context, id + "F6", {"entities" : qUnion([Q0, Q1, Q2, Q3, Q4, Q5]), "operationType" : NewBodyOperationType.REMOVE, "depth" : 24 * mm, "offsetDistance" : 25 * mm, "hasSecondDirection" : true, "secondDirectionOppositeDirection" : false, "secondDirectionDepth" : 23 * mm});
        }
        {
            var Q0;
            {var subQ1=sQuery(id+"F0.wireOp",EDGE,"E18");Q0=makeQuery(id+"F0.imprint","IMPRINT",FACE,{"disambiguationData":[TD([[makeQuery(id+"F0.imprint","IMPRINT",EDGE,{"derivedFrom":subQ1}),1.0]])]});}
            var Q1;
            {var subQ1=sQuery(id+"F0.wireOp",EDGE,"E14");Q1=makeQuery(id+"F0.imprint","IMPRINT",FACE,{"disambiguationData":[TD([[makeQuery(id+"F0.imprint","IMPRINT",EDGE,{"derivedFrom":subQ1}),-1.0]])]});}
            var Q2;
            {var subQ1=sQuery(id+"F0.wireOp",EDGE,"E21");Q2=makeQuery(id+"F0.imprint","IMPRINT",FACE,{"disambiguationData":[TD([[makeQuery(id+"F0.imprint","IMPRINT",EDGE,{"derivedFrom":subQ1}),1.0]])]});}
            var Q3;
            {var subQ1=sQuery(id+"F0.wireOp",EDGE,"E24");Q3=makeQuery(id+"F0.imprint","IMPRINT",FACE,{"disambiguationData":[TD([[makeQuery(id+"F0.imprint","IMPRINT",EDGE,{"derivedFrom":subQ1}),-1.0]])]});}
            extrude(context, id + "F7", {"entities" : qUnion([Q0, Q1, Q2, Q3]), "operationType" : NewBodyOperationType.ADD, "depth" : 3 * mm, "offsetDistance" : 25 * mm});
        }
        {
            var Q0;
            {var subQ0=sQuery(id+"F0.wireOp",EDGE,"E11.top");var subQ1=sQuery(id+"F0.wireOp",EDGE,"E11.bottom");var subQ2=sQuery(id+"F0.wireOp",EDGE,"E0.left");var subQ4=makeQuery(id+"F0.imprint","INTERSECT",VERTEX,{"derivedFrom":[subQ2,sQuery(id+"F0.wireOp",EDGE,"E10.bottom")]});var subQ5=makeQuery(id+"F0.imprint","INTERSECT",VERTEX,{"derivedFrom":[subQ2,sQuery(id+"F0.wireOp",EDGE,"E10.top")]});var subQ6=makeQuery(id+"F0.imprint","INTERSECT",VERTEX,{"derivedFrom":[subQ2,subQ1]});var subQ7=makeQuery(id+"F0.imprint","INTERSECT",VERTEX,{"derivedFrom":[subQ2,subQ0]});Q0=makeQuery(id+"F6.boolean.opBoolean","INTERSECT",EDGE,{"derivedFrom":[makeQuery(id+"F3.boolean.opBoolean","MERGE",FACE,{"derivedFrom":[makeQuery(id+"F2.boolean.opBoolean","COPY",FACE,{"derivedFrom":makeQuery(id+"F2.opExtrude","SWEPT_FACE",FACE,{"disambiguationData":[OSD([subQ2]),TDD([makeQuery(id+"F0.imprint","IMPRINT",EDGE,{"disambiguationData":[TD([[makeQuery(id+"F0.imprint","INTERSECT",VERTEX,{"derivedFrom":[subQ2,sQuery(id+"F0.wireOp",EDGE,"E3")]}),-1.0]])],"derivedFrom":subQ2}),makeQuery(id+"F0.imprint","IMPRINT",EDGE,{"disambiguationData":[TD([[subQ7,-1.0]])],"derivedFrom":subQ2}),makeQuery(id+"F0.imprint","IMPRINT",EDGE,{"disambiguationData":[TD([[subQ6,-1.0]])],"derivedFrom":subQ2}),makeQuery(id+"F0.imprint","IMPRINT",EDGE,{"disambiguationData":[TD([[subQ5,-1.0]])],"derivedFrom":subQ2}),makeQuery(id+"F0.imprint","IMPRINT",EDGE,{"disambiguationData":[TD([[subQ4,-1.0]])],"derivedFrom":subQ2})])]})}),makeQuery(id+"F2.boolean.opBoolean","COPY",FACE,{"derivedFrom":makeQuery(id+"F2.opExtrude","SWEPT_FACE",FACE,{"disambiguationData":[OSD([subQ2]),TDD([makeQuery(id+"F0.imprint","IMPRINT",EDGE,{"disambiguationData":[TD([[makeQuery(id+"F0.imprint","INTERSECT",VERTEX,{"derivedFrom":[sQuery(id+"F0.wireOp",EDGE,"E0.top"),subQ2]}),1.0]])],"derivedFrom":subQ2})])]})}),makeQuery(id+"F3.opExtrude","SWEPT_FACE",FACE,{"disambiguationData":[OSD([subQ2])]})]}),makeQuery(id+"F6.opExtrude","CAP_FACE",FACE,{"disambiguationData":[OSD([subQ1,subQ0,sQuery(id+"F0.wireOp",EDGE,"E11.left"),sQuery(id+"F0.wireOp",EDGE,"E11.right")])],"isStart":false})]});}
            var Q1;
            {var subQ0=sQuery(id+"F0.wireOp",EDGE,"E10.top");var subQ1=sQuery(id+"F0.wireOp",EDGE,"E10.bottom");var subQ2=sQuery(id+"F0.wireOp",EDGE,"E0.left");var subQ4=makeQuery(id+"F0.imprint","INTERSECT",VERTEX,{"derivedFrom":[subQ2,subQ1]});var subQ5=makeQuery(id+"F0.imprint","INTERSECT",VERTEX,{"derivedFrom":[subQ2,subQ0]});var subQ6=makeQuery(id+"F0.imprint","INTERSECT",VERTEX,{"derivedFrom":[subQ2,sQuery(id+"F0.wireOp",EDGE,"E11.bottom")]});var subQ7=makeQuery(id+"F0.imprint","INTERSECT",VERTEX,{"derivedFrom":[subQ2,sQuery(id+"F0.wireOp",EDGE,"E11.top")]});Q1=makeQuery(id+"F6.boolean.opBoolean","INTERSECT",EDGE,{"derivedFrom":[makeQuery(id+"F3.boolean.opBoolean","MERGE",FACE,{"derivedFrom":[makeQuery(id+"F2.boolean.opBoolean","COPY",FACE,{"derivedFrom":makeQuery(id+"F2.opExtrude","SWEPT_FACE",FACE,{"disambiguationData":[OSD([subQ2]),TDD([makeQuery(id+"F0.imprint","IMPRINT",EDGE,{"disambiguationData":[TD([[makeQuery(id+"F0.imprint","INTERSECT",VERTEX,{"derivedFrom":[subQ2,sQuery(id+"F0.wireOp",EDGE,"E3")]}),-1.0]])],"derivedFrom":subQ2}),makeQuery(id+"F0.imprint","IMPRINT",EDGE,{"disambiguationData":[TD([[subQ7,-1.0]])],"derivedFrom":subQ2}),makeQuery(id+"F0.imprint","IMPRINT",EDGE,{"disambiguationData":[TD([[subQ6,-1.0]])],"derivedFrom":subQ2}),makeQuery(id+"F0.imprint","IMPRINT",EDGE,{"disambiguationData":[TD([[subQ5,-1.0]])],"derivedFrom":subQ2}),makeQuery(id+"F0.imprint","IMPRINT",EDGE,{"disambiguationData":[TD([[subQ4,-1.0]])],"derivedFrom":subQ2})])]})}),makeQuery(id+"F2.boolean.opBoolean","COPY",FACE,{"derivedFrom":makeQuery(id+"F2.opExtrude","SWEPT_FACE",FACE,{"disambiguationData":[OSD([subQ2]),TDD([makeQuery(id+"F0.imprint","IMPRINT",EDGE,{"disambiguationData":[TD([[makeQuery(id+"F0.imprint","INTERSECT",VERTEX,{"derivedFrom":[sQuery(id+"F0.wireOp",EDGE,"E0.top"),subQ2]}),1.0]])],"derivedFrom":subQ2})])]})}),makeQuery(id+"F3.opExtrude","SWEPT_FACE",FACE,{"disambiguationData":[OSD([subQ2])]})]}),makeQuery(id+"F6.opExtrude","CAP_FACE",FACE,{"disambiguationData":[OSD([subQ1,subQ0,sQuery(id+"F0.wireOp",EDGE,"E10.left"),sQuery(id+"F0.wireOp",EDGE,"E10.right")])],"isStart":false})]});}
            var Q2;
            {var subQ0=sQuery(id+"F0.wireOp",EDGE,"E0.right");Q2=makeQuery(id+"F6.boolean.opBoolean","INTERSECT",EDGE,{"derivedFrom":[makeQuery(id+"F3.boolean.opBoolean","MERGE",FACE,{"derivedFrom":[makeQuery(id+"F2.boolean.opBoolean","COPY",FACE,{"derivedFrom":makeQuery(id+"F2.opExtrude","SWEPT_FACE",FACE,{"disambiguationData":[OSD([subQ0])]})}),makeQuery(id+"F3.opExtrude","SWEPT_FACE",FACE,{"disambiguationData":[OSD([subQ0])]})]}),makeQuery(id+"F6.opExtrude","CAP_FACE",FACE,{"disambiguationData":[OSD([sQuery(id+"F0.wireOp",EDGE,"E11.bottom"),sQuery(id+"F0.wireOp",EDGE,"E11.top"),sQuery(id+"F0.wireOp",EDGE,"E11.left"),sQuery(id+"F0.wireOp",EDGE,"E11.right")])],"isStart":false})]});}
            var Q3;
            {var subQ0=sQuery(id+"F0.wireOp",EDGE,"E0.right");Q3=makeQuery(id+"F6.boolean.opBoolean","INTERSECT",EDGE,{"derivedFrom":[makeQuery(id+"F3.boolean.opBoolean","MERGE",FACE,{"derivedFrom":[makeQuery(id+"F2.boolean.opBoolean","COPY",FACE,{"derivedFrom":makeQuery(id+"F2.opExtrude","SWEPT_FACE",FACE,{"disambiguationData":[OSD([subQ0])]})}),makeQuery(id+"F3.opExtrude","SWEPT_FACE",FACE,{"disambiguationData":[OSD([subQ0])]})]}),makeQuery(id+"F6.opExtrude","CAP_FACE",FACE,{"disambiguationData":[OSD([sQuery(id+"F0.wireOp",EDGE,"E10.bottom"),sQuery(id+"F0.wireOp",EDGE,"E10.top"),sQuery(id+"F0.wireOp",EDGE,"E10.left"),sQuery(id+"F0.wireOp",EDGE,"E10.right")])],"isStart":false})]});}
            var Q4;
            {var subQ0=sQuery(id+"F0.wireOp",EDGE,"E0.right");Q4=makeQuery(id+"F6.boolean.opBoolean","INTERSECT",EDGE,{"derivedFrom":[makeQuery(id+"F3.boolean.opBoolean","MERGE",FACE,{"derivedFrom":[makeQuery(id+"F2.boolean.opBoolean","COPY",FACE,{"derivedFrom":makeQuery(id+"F2.opExtrude","SWEPT_FACE",FACE,{"disambiguationData":[OSD([subQ0])]})}),makeQuery(id+"F3.opExtrude","SWEPT_FACE",FACE,{"disambiguationData":[OSD([subQ0])]})]}),makeQuery(id+"F6.opExtrude","CAP_FACE",FACE,{"disambiguationData":[OSD([sQuery(id+"F0.wireOp",EDGE,"E11.bottom"),sQuery(id+"F0.wireOp",EDGE,"E11.top"),sQuery(id+"F0.wireOp",EDGE,"E11.left"),sQuery(id+"F0.wireOp",EDGE,"E11.right")])],"isStart":true})]});}
            var Q5;
            {var subQ0=sQuery(id+"F0.wireOp",EDGE,"E0.right");Q5=makeQuery(id+"F6.boolean.opBoolean","INTERSECT",EDGE,{"derivedFrom":[makeQuery(id+"F3.boolean.opBoolean","MERGE",FACE,{"derivedFrom":[makeQuery(id+"F2.boolean.opBoolean","COPY",FACE,{"derivedFrom":makeQuery(id+"F2.opExtrude","SWEPT_FACE",FACE,{"disambiguationData":[OSD([subQ0])]})}),makeQuery(id+"F3.opExtrude","SWEPT_FACE",FACE,{"disambiguationData":[OSD([subQ0])]})]}),makeQuery(id+"F6.opExtrude","CAP_FACE",FACE,{"disambiguationData":[OSD([sQuery(id+"F0.wireOp",EDGE,"E10.bottom"),sQuery(id+"F0.wireOp",EDGE,"E10.top"),sQuery(id+"F0.wireOp",EDGE,"E10.left"),sQuery(id+"F0.wireOp",EDGE,"E10.right")])],"isStart":true})]});}
            var Q6;
            {var subQ0=sQuery(id+"F0.wireOp",EDGE,"E10.top");var subQ1=sQuery(id+"F0.wireOp",EDGE,"E10.bottom");var subQ2=sQuery(id+"F0.wireOp",EDGE,"E0.left");var subQ4=makeQuery(id+"F0.imprint","INTERSECT",VERTEX,{"derivedFrom":[subQ2,subQ1]});var subQ5=makeQuery(id+"F0.imprint","INTERSECT",VERTEX,{"derivedFrom":[subQ2,subQ0]});var subQ6=makeQuery(id+"F0.imprint","INTERSECT",VERTEX,{"derivedFrom":[subQ2,sQuery(id+"F0.wireOp",EDGE,"E11.bottom")]});var subQ7=makeQuery(id+"F0.imprint","INTERSECT",VERTEX,{"derivedFrom":[subQ2,sQuery(id+"F0.wireOp",EDGE,"E11.top")]});Q6=makeQuery(id+"F6.boolean.opBoolean","INTERSECT",EDGE,{"derivedFrom":[makeQuery(id+"F3.boolean.opBoolean","MERGE",FACE,{"derivedFrom":[makeQuery(id+"F2.boolean.opBoolean","COPY",FACE,{"derivedFrom":makeQuery(id+"F2.opExtrude","SWEPT_FACE",FACE,{"disambiguationData":[OSD([subQ2]),TDD([makeQuery(id+"F0.imprint","IMPRINT",EDGE,{"disambiguationData":[TD([[makeQuery(id+"F0.imprint","INTERSECT",VERTEX,{"derivedFrom":[subQ2,sQuery(id+"F0.wireOp",EDGE,"E3")]}),-1.0]])],"derivedFrom":subQ2}),makeQuery(id+"F0.imprint","IMPRINT",EDGE,{"disambiguationData":[TD([[subQ7,-1.0]])],"derivedFrom":subQ2}),makeQuery(id+"F0.imprint","IMPRINT",EDGE,{"disambiguationData":[TD([[subQ6,-1.0]])],"derivedFrom":subQ2}),makeQuery(id+"F0.imprint","IMPRINT",EDGE,{"disambiguationData":[TD([[subQ5,-1.0]])],"derivedFrom":subQ2}),makeQuery(id+"F0.imprint","IMPRINT",EDGE,{"disambiguationData":[TD([[subQ4,-1.0]])],"derivedFrom":subQ2})])]})}),makeQuery(id+"F2.boolean.opBoolean","COPY",FACE,{"derivedFrom":makeQuery(id+"F2.opExtrude","SWEPT_FACE",FACE,{"disambiguationData":[OSD([subQ2]),TDD([makeQuery(id+"F0.imprint","IMPRINT",EDGE,{"disambiguationData":[TD([[makeQuery(id+"F0.imprint","INTERSECT",VERTEX,{"derivedFrom":[sQuery(id+"F0.wireOp",EDGE,"E0.top"),subQ2]}),1.0]])],"derivedFrom":subQ2})])]})}),makeQuery(id+"F3.opExtrude","SWEPT_FACE",FACE,{"disambiguationData":[OSD([subQ2])]})]}),makeQuery(id+"F6.opExtrude","CAP_FACE",FACE,{"disambiguationData":[OSD([subQ1,subQ0,sQuery(id+"F0.wireOp",EDGE,"E10.left"),sQuery(id+"F0.wireOp",EDGE,"E10.right")])],"isStart":true})]});}
            var Q7;
            {var subQ0=sQuery(id+"F0.wireOp",EDGE,"E11.top");var subQ1=sQuery(id+"F0.wireOp",EDGE,"E11.bottom");var subQ2=sQuery(id+"F0.wireOp",EDGE,"E0.left");var subQ4=makeQuery(id+"F0.imprint","INTERSECT",VERTEX,{"derivedFrom":[subQ2,sQuery(id+"F0.wireOp",EDGE,"E10.bottom")]});var subQ5=makeQuery(id+"F0.imprint","INTERSECT",VERTEX,{"derivedFrom":[subQ2,sQuery(id+"F0.wireOp",EDGE,"E10.top")]});var subQ6=makeQuery(id+"F0.imprint","INTERSECT",VERTEX,{"derivedFrom":[subQ2,subQ1]});var subQ7=makeQuery(id+"F0.imprint","INTERSECT",VERTEX,{"derivedFrom":[subQ2,subQ0]});Q7=makeQuery(id+"F6.boolean.opBoolean","INTERSECT",EDGE,{"derivedFrom":[makeQuery(id+"F3.boolean.opBoolean","MERGE",FACE,{"derivedFrom":[makeQuery(id+"F2.boolean.opBoolean","COPY",FACE,{"derivedFrom":makeQuery(id+"F2.opExtrude","SWEPT_FACE",FACE,{"disambiguationData":[OSD([subQ2]),TDD([makeQuery(id+"F0.imprint","IMPRINT",EDGE,{"disambiguationData":[TD([[makeQuery(id+"F0.imprint","INTERSECT",VERTEX,{"derivedFrom":[subQ2,sQuery(id+"F0.wireOp",EDGE,"E3")]}),-1.0]])],"derivedFrom":subQ2}),makeQuery(id+"F0.imprint","IMPRINT",EDGE,{"disambiguationData":[TD([[subQ7,-1.0]])],"derivedFrom":subQ2}),makeQuery(id+"F0.imprint","IMPRINT",EDGE,{"disambiguationData":[TD([[subQ6,-1.0]])],"derivedFrom":subQ2}),makeQuery(id+"F0.imprint","IMPRINT",EDGE,{"disambiguationData":[TD([[subQ5,-1.0]])],"derivedFrom":subQ2}),makeQuery(id+"F0.imprint","IMPRINT",EDGE,{"disambiguationData":[TD([[subQ4,-1.0]])],"derivedFrom":subQ2})])]})}),makeQuery(id+"F2.boolean.opBoolean","COPY",FACE,{"derivedFrom":makeQuery(id+"F2.opExtrude","SWEPT_FACE",FACE,{"disambiguationData":[OSD([subQ2]),TDD([makeQuery(id+"F0.imprint","IMPRINT",EDGE,{"disambiguationData":[TD([[makeQuery(id+"F0.imprint","INTERSECT",VERTEX,{"derivedFrom":[sQuery(id+"F0.wireOp",EDGE,"E0.top"),subQ2]}),1.0]])],"derivedFrom":subQ2})])]})}),makeQuery(id+"F3.opExtrude","SWEPT_FACE",FACE,{"disambiguationData":[OSD([subQ2])]})]}),makeQuery(id+"F6.opExtrude","CAP_FACE",FACE,{"disambiguationData":[OSD([subQ1,subQ0,sQuery(id+"F0.wireOp",EDGE,"E11.left"),sQuery(id+"F0.wireOp",EDGE,"E11.right")])],"isStart":true})]});}
            var Q8;
            Q8=makeQuery(id+"F2.boolean.opBoolean","COPY",EDGE,{"derivedFrom":makeQuery(id+"F2.opExtrude","CAP_EDGE",EDGE,{"disambiguationData":[OSD([sQuery(id+"F0.wireOp",EDGE,"E3")])],"isStart":false})});
            var Q9;
            Q9=makeQuery(id+"F2.boolean.opBoolean","COPY",EDGE,{"derivedFrom":makeQuery(id+"F2.opExtrude","CAP_EDGE",EDGE,{"disambiguationData":[OSD([sQuery(id+"F0.wireOp",EDGE,"E4")])],"isStart":false})});
            var Q10;
            {var subQ0=sQuery(id+"F0.wireOp",EDGE,"E7");Q10=makeQuery(id+"F2.boolean.opBoolean","COPY",EDGE,{"derivedFrom":makeQuery(id+"F2.opExtrude","CAP_EDGE",EDGE,{"disambiguationData":[OSD([subQ0]),TDD([makeQuery(id+"F0.imprint","IMPRINT",EDGE,{"disambiguationData":[TD([[makeQuery(id+"F0.imprint","INTERSECT",VERTEX,{"disambiguationData":[OD(0.0)],"derivedFrom":[sQuery(id+"F0.wireOp",EDGE,"E0.left"),subQ0]}),1.0]])],"derivedFrom":subQ0})])],"isStart":false})});}
            var Q11;
            Q11=makeQuery(id+"F2.boolean.opBoolean","COPY",EDGE,{"derivedFrom":makeQuery(id+"F2.opExtrude","CAP_EDGE",EDGE,{"disambiguationData":[OSD([sQuery(id+"F0.wireOp",EDGE,"E8")])],"isStart":false})});
            var Q12;
            Q12=makeQuery(id+"F2.boolean.opBoolean","COPY",FACE,{"derivedFrom":makeQuery(id+"F2.opExtrude","CAP_FACE",FACE,{"disambiguationData":[OSD([sQuery(id+"F0.wireOp",EDGE,"E0.bottom"),sQuery(id+"F0.wireOp",EDGE,"E0.left"),sQuery(id+"F0.wireOp",EDGE,"E0.right"),sQuery(id+"F0.wireOp",EDGE,"E3"),sQuery(id+"F0.wireOp",EDGE,"E4"),sQuery(id+"F0.wireOp",EDGE,"E7"),sQuery(id+"F0.wireOp",EDGE,"E8"),sQuery(id+"F0.wireOp",EDGE,"E12.top")])],"isStart":true})});
            var Q13;
            {var subQ0=sQuery(id+"F0.wireOp",EDGE,"E9.right");Q13=makeQuery(id+"F7.opExtrude","CAP_EDGE",EDGE,{"disambiguationData":[OSD([subQ0]),TDD([makeQuery(id+"F0.imprint","IMPRINT",EDGE,{"disambiguationData":[TD([[makeQuery(id+"F0.imprint","INTERSECT",VERTEX,{"derivedFrom":[subQ0,sQuery(id+"F0.wireOp",EDGE,"E23")]}),-1.0]])],"derivedFrom":subQ0})])],"isStart":false});}
            var Q14;
            {var subQ0=sQuery(id+"F0.wireOp",EDGE,"E9.right");Q14=makeQuery(id+"F7.opExtrude","CAP_EDGE",EDGE,{"disambiguationData":[OSD([subQ0]),TDD([makeQuery(id+"F0.imprint","IMPRINT",EDGE,{"disambiguationData":[TD([[makeQuery(id+"F0.imprint","INTERSECT",VERTEX,{"derivedFrom":[subQ0,sQuery(id+"F0.wireOp",EDGE,"E16")]}),1.0]])],"derivedFrom":subQ0})])],"isStart":false});}
            var Q15;
            {var subQ0=sQuery(id+"F0.wireOp",EDGE,"E9.left");Q15=makeQuery(id+"F7.opExtrude","CAP_EDGE",EDGE,{"disambiguationData":[OSD([subQ0]),TDD([makeQuery(id+"F0.imprint","IMPRINT",EDGE,{"disambiguationData":[TD([[makeQuery(id+"F0.imprint","INTERSECT",VERTEX,{"derivedFrom":[subQ0,sQuery(id+"F0.wireOp",EDGE,"E20")]}),1.0]])],"derivedFrom":subQ0})])],"isStart":false});}
            var Q16;
            {var subQ0=sQuery(id+"F0.wireOp",EDGE,"E9.left");Q16=makeQuery(id+"F7.opExtrude","CAP_EDGE",EDGE,{"disambiguationData":[OSD([subQ0]),TDD([makeQuery(id+"F0.imprint","IMPRINT",EDGE,{"disambiguationData":[TD([[makeQuery(id+"F0.imprint","INTERSECT",VERTEX,{"derivedFrom":[subQ0,sQuery(id+"F0.wireOp",EDGE,"E26")]}),-1.0]])],"derivedFrom":subQ0})])],"isStart":false});}
            var Q17;
            Q17=makeQuery(id+"F1.opExtrude","SWEPT_EDGE",EDGE,{"disambiguationData":[OSD([sQuery(id+"F0.wireOp",EDGE,"E9.top"),sQuery(id+"F0.wireOp",EDGE,"E9.right"),sQuery(id+"F0.wireOp",EDGE,"E21")])]});
            var Q18;
            Q18=makeQuery(id+"F1.opExtrude","SWEPT_EDGE",EDGE,{"disambiguationData":[OSD([sQuery(id+"F0.wireOp",EDGE,"E9.top"),sQuery(id+"F0.wireOp",EDGE,"E9.left"),sQuery(id+"F0.wireOp",EDGE,"E24")])]});
            var Q19;
            Q19=makeQuery(id+"F1.opExtrude","SWEPT_EDGE",EDGE,{"disambiguationData":[OSD([sQuery(id+"F0.wireOp",EDGE,"E9.bottom"),sQuery(id+"F0.wireOp",EDGE,"E9.left"),sQuery(id+"F0.wireOp",EDGE,"E18")])]});
            var Q20;
            Q20=makeQuery(id+"F1.opExtrude","SWEPT_EDGE",EDGE,{"disambiguationData":[OSD([sQuery(id+"F0.wireOp",EDGE,"E9.bottom"),sQuery(id+"F0.wireOp",EDGE,"E9.right"),sQuery(id+"F0.wireOp",EDGE,"E14")])]});
            var Q21;
            {var subQ0=sQuery(id+"F0.wireOp",EDGE,"E9.right");var subQ1=sQuery(id+"F0.wireOp",EDGE,"E9.left");Q21=makeQuery(id+"F7.boolean.opBoolean","MERGE",FACE,{"derivedFrom":[makeQuery(id+"F1.opExtrude","CAP_FACE",FACE,{"disambiguationData":[OSD([sQuery(id+"F0.wireOp",EDGE,"E9.bottom"),sQuery(id+"F0.wireOp",EDGE,"E9.top"),subQ1,subQ0])],"isStart":true}),makeQuery(id+"F7.opExtrude","CAP_FACE",FACE,{"disambiguationData":[OSD([subQ1,sQuery(id+"F0.wireOp",EDGE,"E18"),sQuery(id+"F0.wireOp",EDGE,"E19"),sQuery(id+"F0.wireOp",EDGE,"E20"),sQuery(id+"F0.wireOp",EDGE,"E27")])],"isStart":true}),makeQuery(id+"F7.opExtrude","CAP_FACE",FACE,{"disambiguationData":[OSD([subQ1,sQuery(id+"F0.wireOp",EDGE,"E24"),sQuery(id+"F0.wireOp",EDGE,"E25"),sQuery(id+"F0.wireOp",EDGE,"E26"),sQuery(id+"F0.wireOp",EDGE,"E28")])],"isStart":true}),makeQuery(id+"F7.opExtrude","CAP_FACE",FACE,{"disambiguationData":[OSD([subQ0,sQuery(id+"F0.wireOp",EDGE,"E14"),sQuery(id+"F0.wireOp",EDGE,"E15"),sQuery(id+"F0.wireOp",EDGE,"E16"),sQuery(id+"F0.wireOp",EDGE,"E17")])],"isStart":true}),makeQuery(id+"F7.opExtrude","CAP_FACE",FACE,{"disambiguationData":[OSD([subQ0,sQuery(id+"F0.wireOp",EDGE,"E21"),sQuery(id+"F0.wireOp",EDGE,"E22"),sQuery(id+"F0.wireOp",EDGE,"E23"),sQuery(id+"F0.wireOp",EDGE,"E29")])],"isStart":true})]});}
            var Q22;
            Q22=makeQuery(id+"F7.opExtrude","CAP_FACE",FACE,{"disambiguationData":[OSD([sQuery(id+"F0.wireOp",EDGE,"E9.right"),sQuery(id+"F0.wireOp",EDGE,"E21"),sQuery(id+"F0.wireOp",EDGE,"E22"),sQuery(id+"F0.wireOp",EDGE,"E23"),sQuery(id+"F0.wireOp",EDGE,"E29")])],"isStart":false});
            var Q23;
            Q23=makeQuery(id+"F7.opExtrude","CAP_FACE",FACE,{"disambiguationData":[OSD([sQuery(id+"F0.wireOp",EDGE,"E9.left"),sQuery(id+"F0.wireOp",EDGE,"E24"),sQuery(id+"F0.wireOp",EDGE,"E25"),sQuery(id+"F0.wireOp",EDGE,"E26"),sQuery(id+"F0.wireOp",EDGE,"E28")])],"isStart":false});
            var Q24;
            Q24=makeQuery(id+"F7.opExtrude","CAP_FACE",FACE,{"disambiguationData":[OSD([sQuery(id+"F0.wireOp",EDGE,"E9.left"),sQuery(id+"F0.wireOp",EDGE,"E18"),sQuery(id+"F0.wireOp",EDGE,"E19"),sQuery(id+"F0.wireOp",EDGE,"E20"),sQuery(id+"F0.wireOp",EDGE,"E27")])],"isStart":false});
            var Q25;
            Q25=makeQuery(id+"F7.opExtrude","CAP_FACE",FACE,{"disambiguationData":[OSD([sQuery(id+"F0.wireOp",EDGE,"E9.right"),sQuery(id+"F0.wireOp",EDGE,"E14"),sQuery(id+"F0.wireOp",EDGE,"E15"),sQuery(id+"F0.wireOp",EDGE,"E16"),sQuery(id+"F0.wireOp",EDGE,"E17")])],"isStart":false});
            var Q26;
            Q26=makeQuery(id+"F3.boolean.opBoolean","COPY",EDGE,{"derivedFrom":makeQuery(id+"F3.opExtrude","CAP_EDGE",EDGE,{"disambiguationData":[OSD([sQuery(id+"F0.wireOp",EDGE,"E0.bottom")])],"isStart":false})});
            var Q27;
            Q27=makeQuery(id+"F3.boolean.opBoolean","COPY",EDGE,{"derivedFrom":makeQuery(id+"F3.opExtrude","CAP_EDGE",EDGE,{"disambiguationData":[OSD([sQuery(id+"F0.wireOp",EDGE,"E0.right")])],"isStart":false})});
            var Q28;
            Q28=makeQuery(id+"F3.boolean.opBoolean","COPY",EDGE,{"derivedFrom":makeQuery(id+"F3.opExtrude","CAP_EDGE",EDGE,{"disambiguationData":[OSD([sQuery(id+"F0.wireOp",EDGE,"E0.left")])],"isStart":false})});
            var Q29;
            {var subQ0=sQuery(id+"F0.wireOp",EDGE,"E0.left");var subQ1=sQuery(id+"F0.wireOp",EDGE,"E0.top");var subQ3=sQuery(id+"F0.wireOp",EDGE,"E12.top");Q29=makeQuery(id+"F5.boolean.opBoolean","SPLIT",EDGE,{"disambiguationData":[TD([makeQuery(id+"F3.opExtrude","SWEPT_FACE",FACE,{"disambiguationData":[OSD([subQ0])]})])],"derivedFrom":makeQuery(id+"F3.boolean.opBoolean","COPY",EDGE,{"derivedFrom":makeQuery(id+"F3.opExtrude","CAP_EDGE",EDGE,{"disambiguationData":[OSD([subQ1,subQ3])],"isStart":false})})});}
            var Q30;
            {var subQ0=sQuery(id+"F0.wireOp",EDGE,"E12.top");var subQ1=sQuery(id+"F0.wireOp",EDGE,"E0.right");var subQ2=sQuery(id+"F0.wireOp",EDGE,"E0.top");Q30=makeQuery(id+"F5.boolean.opBoolean","SPLIT",EDGE,{"disambiguationData":[TD([makeQuery(id+"F2.boolean.opBoolean","COPY",FACE,{"derivedFrom":makeQuery(id+"F2.opExtrude","SWEPT_FACE",FACE,{"disambiguationData":[OSD([subQ1])]})})])],"derivedFrom":makeQuery(id+"F3.boolean.opBoolean","COPY",EDGE,{"derivedFrom":makeQuery(id+"F3.opExtrude","CAP_EDGE",EDGE,{"disambiguationData":[OSD([subQ2,subQ0])],"isStart":false})})});}
            var Q31;
            Q31=makeQuery(id+"F4.boolean.opBoolean","INTERSECT",EDGE,{"derivedFrom":[makeQuery(id+"F1.opExtrude","SWEPT_FACE",FACE,{"disambiguationData":[OSD([sQuery(id+"F0.wireOp",EDGE,"E9.top")])]}),makeQuery(id+"F4.opExtrude","CAP_FACE",FACE,{"disambiguationData":[OSD([sQuery(id+"F0.wireOp",EDGE,"E12.bottom"),sQuery(id+"F0.wireOp",EDGE,"E12.top"),sQuery(id+"F0.wireOp",EDGE,"E12.left"),sQuery(id+"F0.wireOp",EDGE,"E12.right")])],"isStart":true})]});
            var Q32;
            Q32=makeQuery(id+"F4.boolean.opBoolean","INTERSECT",EDGE,{"derivedFrom":[makeQuery(id+"F1.opExtrude","SWEPT_FACE",FACE,{"disambiguationData":[OSD([sQuery(id+"F0.wireOp",EDGE,"E9.top")])]}),makeQuery(id+"F4.opExtrude","SWEPT_FACE",FACE,{"disambiguationData":[OSD([sQuery(id+"F0.wireOp",EDGE,"E12.right")])]})]});
            var Q33;
            Q33=makeQuery(id+"F4.boolean.opBoolean","INTERSECT",EDGE,{"derivedFrom":[makeQuery(id+"F1.opExtrude","SWEPT_FACE",FACE,{"disambiguationData":[OSD([sQuery(id+"F0.wireOp",EDGE,"E9.top")])]}),makeQuery(id+"F4.opExtrude","SWEPT_FACE",FACE,{"disambiguationData":[OSD([sQuery(id+"F0.wireOp",EDGE,"E12.left")])]})]});
            chamfer(context, id + "F8", {"entities" : qUnion([Q0, Q1, Q2, Q3, Q4, Q5, Q6, Q7, Q8, Q9, Q10, Q11, Q12, Q13, Q14, Q15, Q16, Q17, Q18, Q19, Q20, Q21, Q22, Q23, Q24, Q25, Q26, Q27, Q28, Q29, Q30, Q31, Q32, Q33]), "width" : 0.5 * mm, "tangentPropagation" : true});
        }
    });
